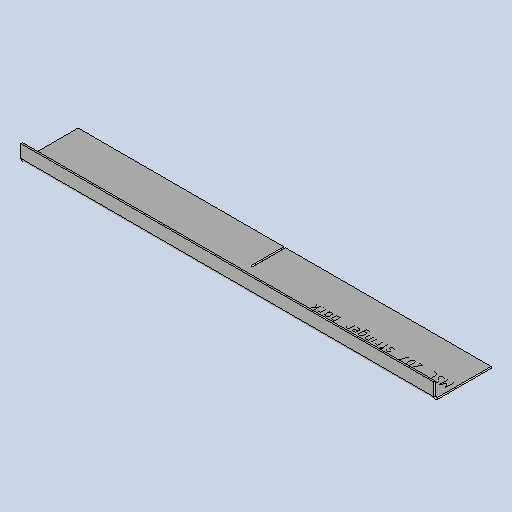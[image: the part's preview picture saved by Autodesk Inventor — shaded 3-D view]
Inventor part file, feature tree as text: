
AUTODESK INVENTOR PART (.ipt)
format: ipt  version: 2025 (Build 290162010, 162A)  size: 286,720 bytes
history: native  units: mm
features: other x5, sheet_metal_op x4, sketch x4, extrude x1
ambient origin geometry x8: Origin, YZ Plane, XZ Plane, XY Plane, X Axis, Y Axis, Z Axis, Center Point
bodies: Solid1 (feature_tree)
feature tree (14):
  sheet_metal_op  "Face1"
  sheet_metal_op  "Flange1"
  extrude  "Extrusion1"  Depth=68.0mm
  other  "Mark2"
  other  "A-Side Definition"
  sketch  "Sketch1"  dims[d0=980.0mm d1=68.0mm]
  other  "Plate1"
  sketch  "Sketch2"  dims[d2=2.0mm]
  other  "Plate2"
  sheet_metal_op  "Bend1"
  sheet_metal_op  "Corner1"
  sketch  "Sketch5"  dims[d3=2.0mm]
  sketch  "Sketch9"  dims[d4=1.0mm d5=4.0mm d6=2.75mm d7=20.0mm d8=90.0deg d9=2.75mm d10=8.0mm d11=2.0mm d12=2.75mm d15=0.0mm d16=0.0mm d40=200.0mm d41=12.0mm d45=70.0mm d48=2.1mm d49=490.0mm d51=29.0mm d52=39.0mm]
  other  "Definition1"
